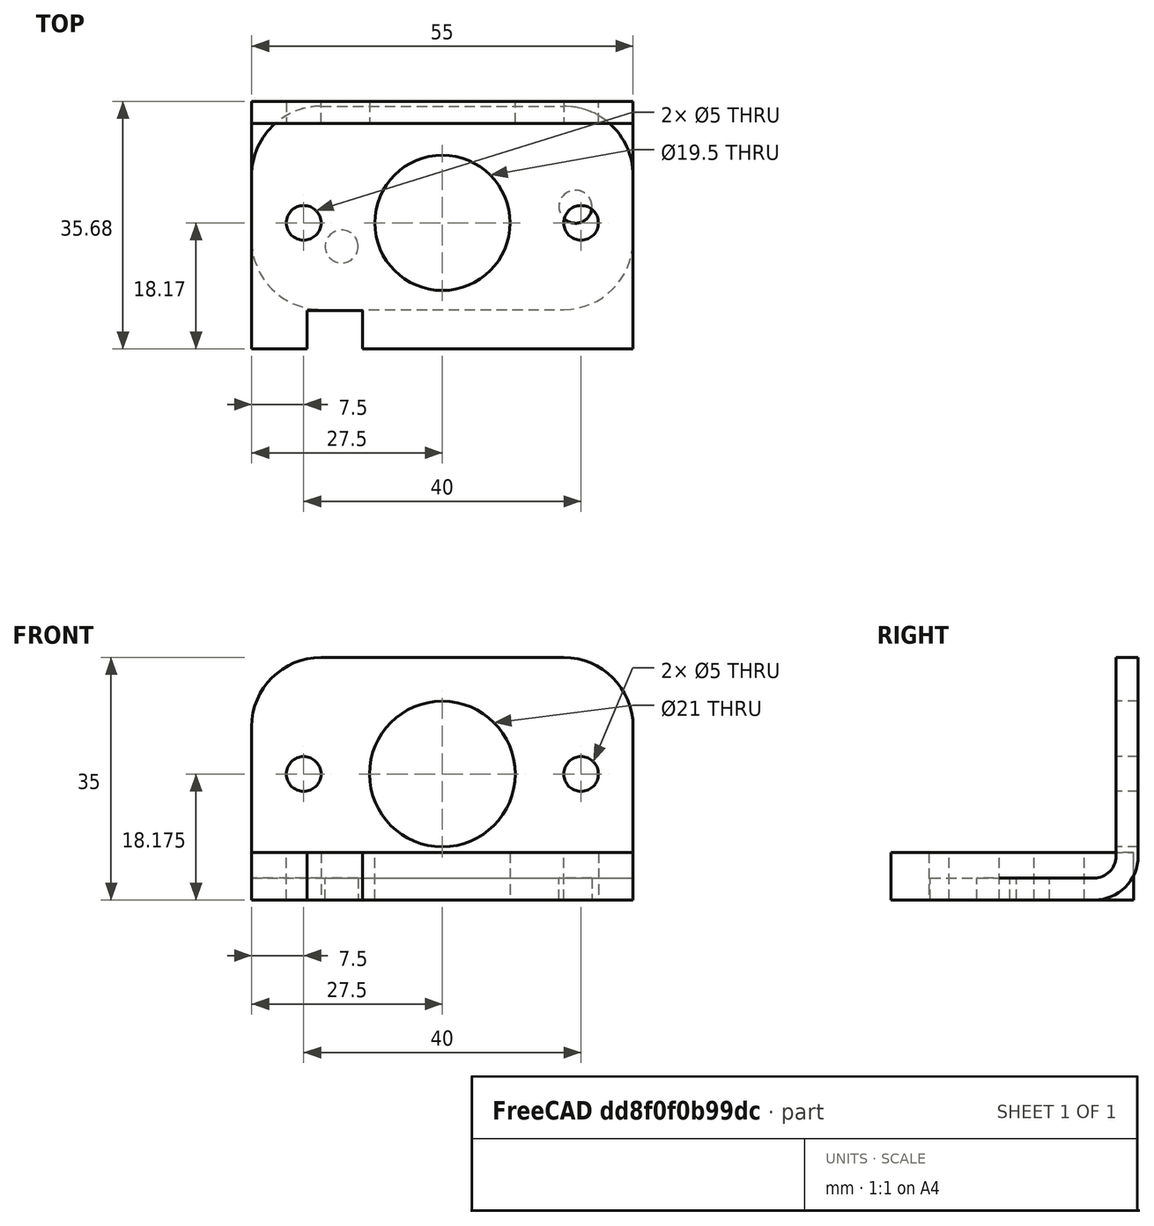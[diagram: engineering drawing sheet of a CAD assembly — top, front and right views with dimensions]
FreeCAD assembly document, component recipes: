
FREECAD ASSEMBLY — COMPONENT RECIPES ("RudderPedalBracketAssembly")

This assembly document has 4 components, labeled P0..P3 below (a component is one placed body or linked part). 4 of them carry a construction recipe — the FreeCAD feature program that regenerates the part from scratch, quoted from this document or its linked companion documents; the rest are supplied as boundary geometry only. No exploded tour is included for this assembly.
COMPONENT P0 — recipe-attached ("LeftBearing", modeled in this document).
Construction recipe (the document's own serialized feature program — sketch geometry with constraints, then the solid features built on it; lengths are millimeters unless a unit is written):

FEATURE [PartDesign::FeaturePython] BaseShape001  # WARN: FeaturePython — macro-defined, semantics opaque (R4)
  Suppressed = false
  fillGaps = true
  flangeWidth = 5
  height = 10
  length = 55
  originLoc = 4
  radius = 1
  shapeType = 0
  thickness = 6.858
  width = 35
FEATURE [Sketcher::SketchObject] Sketch002
  ArcFitTolerance = 1e-06
  AttachmentSupport = -> [BaseShape001]
  ExternalGeometry = -> [BaseShape001]
  FullyConstrained = true
  MakeInternals = false
  MapMode = 5
  Placement = pos=(0,0,6.858) rot=(0,0,1;0rad)
  sketch-geometry (7):
    g0: Circle CenterX=0 CenterY=0.67 CenterZ=0 NormalX=0 NormalY=0 NormalZ=1 AngleXU=0 Radius=9.75
    g1: Circle CenterX=-20 CenterY=0.67 CenterZ=0 NormalX=0 NormalY=0 NormalZ=1 AngleXU=0 Radius=2.5
    g2: Circle CenterX=20 CenterY=0.67 CenterZ=0 NormalX=0 NormalY=0 NormalZ=1 AngleXU=0 Radius=2.5
    g3: LineSegment StartX=-19.5 StartY=-17.5 StartZ=0 EndX=-11.5 EndY=-17.5 EndZ=0
    g4: LineSegment StartX=-11.5 StartY=-17.5 StartZ=0 EndX=-11.5 EndY=-12 EndZ=0
    g5: LineSegment StartX=-11.5 StartY=-12 StartZ=0 EndX=-19.5 EndY=-12 EndZ=0
    g6: LineSegment StartX=-19.5 StartY=-12 StartZ=0 EndX=-19.5 EndY=-17.5 EndZ=0
  constraints (21):
    c: Diameter(g0) = 19.5
    c: Diameter(g1) = 5
    c: Diameter(g2) = 5
    c: DistanceX(g1,g0) = 20
    c: DistanceX(g0,g2) = 20
    c: DistanceY(g-3,g0) = 18.17
    c: Vertical(g0,g-1)
    c: Horizontal(g1,g0)
    c: Horizontal(g2,g0)
    c: Coincident(g3,g4)
    c: Coincident(g4,g5)
    c: Coincident(g5,g6)
    c: Coincident(g6,g3)
    c: Horizontal(g3)
    c: Horizontal(g5)
    c: Vertical(g4)
    c: Vertical(g6)
    c: PointOnObject(g3,g-3)
    c: DistanceX(g-3,g3) = 8
    c: DistanceY(g3,g5) = 5.5
    c: DistanceX(g3,g3) = 8
FEATURE [PartDesign::Pocket] Pocket001
  BaseFeature = -> BaseShape001
  Direction = (0,0,-1)
  Length = 5
  Length2 = 5
  Profile = -> Sketch002
  ReferenceAxis = -> Sketch002 [N_Axis]
  Refine = true
  Suppressed = false
  Type = 1
FEATURE [PartDesign::Fillet] Fillet002
  Base = -> Pocket001 [Edge3,Edge18]
  BaseFeature = -> Pocket001
  Radius = 10
  Refine = true
  SupportTransform = false
  Suppressed = false
  UseAllEdges = false
FEATURE [PartDesign::Body] Body001  label="Bearing"
  AllowCompound = false
  Group = -> [BaseShape001,Sketch002,Pocket001,Fillet002]
  Origin = -> Origin002
  Tip = -> Fillet002
COMPONENT P1 — same part as P0; its construction recipe is shown at P0.
COMPONENT P2 — recipe-attached ("LeftBracket001", modeled in this document).
Construction recipe (the document's own serialized feature program — sketch geometry with constraints, then the solid features built on it; lengths are millimeters unless a unit is written):

FEATURE [PartDesign::FeaturePython] BaseShape  # WARN: FeaturePython — macro-defined, semantics opaque (R4)
  Suppressed = false
  fillGaps = true
  flangeWidth = 5
  height = 35
  length = 55
  originLoc = 4
  radius = 3.175
  shapeType = 1
  thickness = 3.175
  width = 30
FEATURE [Sketcher::SketchObject] Sketch001
  ArcFitTolerance = 1e-06
  FullyConstrained = true
  MakeInternals = false
  MapMode = 5
  Placement = pos=(0,15,0) rot=(1,0,0;1.5708rad)
  sketch-geometry (3):
    g0: Circle CenterX=0 CenterY=18.175 CenterZ=0 NormalX=0 NormalY=0 NormalZ=1 AngleXU=0 Radius=10.5
    g1: Circle CenterX=-20 CenterY=18.175 CenterZ=0 NormalX=0 NormalY=0 NormalZ=1 AngleXU=0 Radius=2.5
    g2: Circle CenterX=20 CenterY=18.175 CenterZ=0 NormalX=0 NormalY=0 NormalZ=1 AngleXU=0 Radius=2.5
  constraints (9):
    c: Diameter(g0) = 21
    c: PointOnObject(g0,g-2)
    c: DistanceY(g-3,g0) = 15
    c: Diameter(g1) = 5
    c: Diameter(g2) = 5
    c: Horizontal(g0,g2)
    c: Horizontal(g1,g0)
    c: DistanceX(g1,g0) = 20
    c: DistanceX(g0,g2) = 20
FEATURE [Sketcher::SketchObject] Sketch
  ArcFitTolerance = 1e-06
  AttachmentSupport = -> [BaseShape]
  ExternalGeometry = -> [BaseShape]
  FullyConstrained = true
  MakeInternals = false
  MapMode = 5
  Placement = pos=(0,0,3.175) rot=(0,0,1;0rad)
  sketch-geometry (2):
    g0: Circle CenterX=-17.437 CenterY=3 CenterZ=0 NormalX=0 NormalY=0 NormalZ=1 AngleXU=0 Radius=2.3815
    g1: Circle CenterX=16.272 CenterY=-2.735 CenterZ=0 NormalX=0 NormalY=0 NormalZ=1 AngleXU=0 Radius=2.3815
  constraints (6):
    c: Diameter(g0) = 4.763
    c: Diameter(g1) = 4.763
    c: DistanceX(g0,g1) = 33.709
    c: DistanceY(g1,g0) = 5.735
    c: DistanceX(g0,g-1) = 17.437
    c: DistanceY(g0,g-3) = 12
FEATURE [PartDesign::Pocket] Pocket004  label="PocketBase"
  BaseFeature = -> BaseShape
  Direction = (0,0,-1)
  Length = 5
  Length2 = 5
  Profile = -> Sketch
  ReferenceAxis = -> Sketch [N_Axis]
  Refine = true
  Suppressed = false
  Type = 1
FEATURE [PartDesign::Pocket] Pocket  label="PocketUpper"
  BaseFeature = -> Pocket004
  Direction = (0,1,-2e-16)
  Length = 5
  Length2 = 5
  Profile = -> Sketch001
  ReferenceAxis = -> Sketch001 [N_Axis]
  Refine = true
  Suppressed = false
  Type = 1
FEATURE [PartDesign::Fillet] Fillet
  Base = -> Pocket [Edge22,Edge12,Edge2,Edge4]
  BaseFeature = -> Pocket
  Radius = 10
  Refine = true
  SupportTransform = false
  Suppressed = false
  UseAllEdges = false
FEATURE [PartDesign::Body] Body  label="LeftBracket"
  AllowCompound = false
  Group = -> [BaseShape,Pocket004,Sketch,Sketch001,Pocket,Fillet]
  Origin = -> Origin
  Tip = -> Fillet
COMPONENT P3 — recipe-attached ("RightBracket001", modeled in this document).
Construction recipe (the document's own serialized feature program — sketch geometry with constraints, then the solid features built on it; lengths are millimeters unless a unit is written):

FEATURE [PartDesign::FeaturePython] BaseShape002  # WARN: FeaturePython — macro-defined, semantics opaque (R4)
  Suppressed = false
  fillGaps = true
  flangeWidth = 5
  height = 35
  length = 55
  originLoc = 4
  radius = 3.175
  shapeType = 1
  thickness = 3.175
  width = 30
FEATURE [Sketcher::SketchObject] Sketch003
  ArcFitTolerance = 1e-06
  AttachmentSupport = -> [BaseShape002]
  ExternalGeometry = -> [BaseShape002]
  FullyConstrained = true
  MakeInternals = false
  MapMode = 5
  Placement = pos=(0,0,3.175) rot=(0,0,1;0rad)
  sketch-geometry (2):
    g0: Circle CenterX=-14.523 CenterY=-2.74 CenterZ=0 NormalX=0 NormalY=0 NormalZ=1 AngleXU=0 Radius=2.38125
    g1: Circle CenterX=19.186 CenterY=3 CenterZ=0 NormalX=0 NormalY=0 NormalZ=1 AngleXU=0 Radius=2.38125
  constraints (6):
    c: Diameter(g0) = 4.7625
    c: Diameter(g1) = 4.7625
    c: DistanceY(g1,g-3) = 12
    c: DistanceX(g0,g1) = 33.709
    c: DistanceX(g0,g-1) = 14.523
    c: DistanceY(g0,g1) = 5.74
FEATURE [PartDesign::Pocket] Pocket002  label="PocketBase001"
  BaseFeature = -> BaseShape002
  Direction = (0,0,-1)
  Length = 5
  Length2 = 5
  Profile = -> Sketch003
  ReferenceAxis = -> Sketch003 [N_Axis]
  Refine = true
  Suppressed = false
  Type = 1
FEATURE [Sketcher::SketchObject] Sketch004
  ArcFitTolerance = 1e-06
  AttachmentSupport = -> [Pocket002]
  ExternalGeometry = -> [Pocket002]
  FullyConstrained = true
  MakeInternals = false
  MapMode = 5
  Placement = pos=(0,15,0) rot=(1,0,0;1.5708rad)
  sketch-geometry (3):
    g0: Circle CenterX=0 CenterY=18.175 CenterZ=0 NormalX=0 NormalY=0 NormalZ=1 AngleXU=0 Radius=10.5
    g1: Circle CenterX=-20 CenterY=18.175 CenterZ=0 NormalX=0 NormalY=0 NormalZ=1 AngleXU=0 Radius=2.5
    g2: Circle CenterX=20 CenterY=18.175 CenterZ=0 NormalX=0 NormalY=0 NormalZ=1 AngleXU=0 Radius=2.5
  constraints (9):
    c: Diameter(g0) = 21
    c: Diameter(g1) = 5
    c: Diameter(g2) = 5
    c: Horizontal(g1,g0)
    c: Horizontal(g0,g2)
    c: DistanceX(g1,g0) = 20
    c: DistanceX(g0,g2) = 20
    c: DistanceY(g-3,g0) = 15
    c: Vertical(g0,g-1)
FEATURE [PartDesign::Pocket] Pocket003  label="PocketUpper001"
  BaseFeature = -> Pocket002
  Direction = (0,1,-2e-16)
  Length = 5
  Length2 = 5
  Profile = -> Sketch004
  ReferenceAxis = -> Sketch004 [N_Axis]
  Refine = true
  Suppressed = false
  Type = 1
FEATURE [PartDesign::Fillet] Fillet001
  Base = -> Pocket003 [Edge22,Edge12,Edge2,Edge4]
  BaseFeature = -> Pocket003
  Radius = 10
  Refine = true
  SupportTransform = false
  Suppressed = false
  UseAllEdges = false
FEATURE [PartDesign::Body] Body002  label="RightBracket"
  AllowCompound = false
  Group = -> [BaseShape002,Sketch003,Pocket002,Sketch004,Pocket003,Fillet001]
  Origin = -> Origin003
  Tip = -> Fillet001
PROVENANCE & LICENSES
A FreeCAD (.FCStd) document from a public repository crawl; recipes are the document's own serialized feature recipes (and, for linked parts, companion documents' recipes).
License: as declared in the source repository (recorded in the dataset sidecar).
